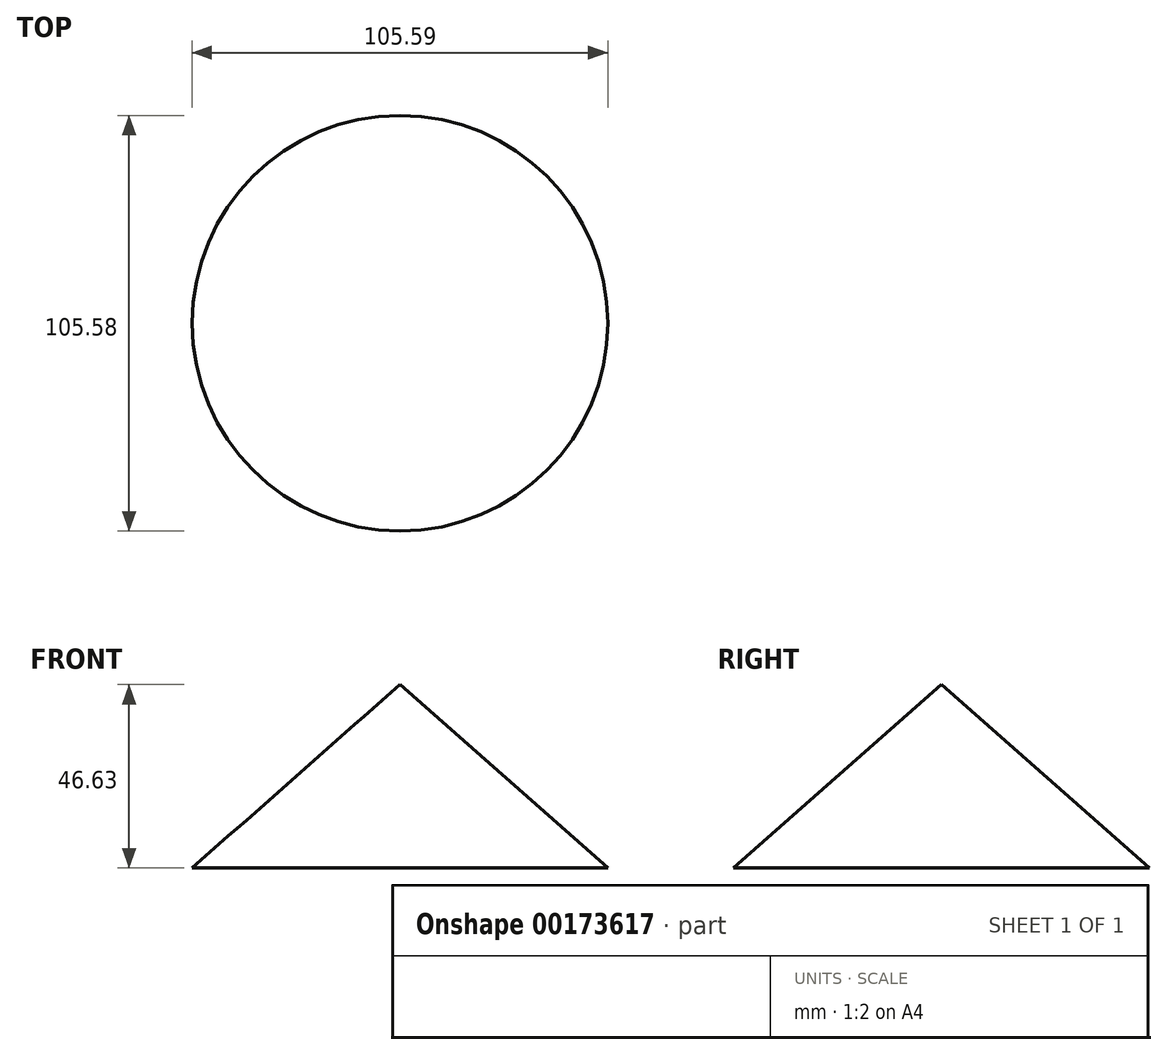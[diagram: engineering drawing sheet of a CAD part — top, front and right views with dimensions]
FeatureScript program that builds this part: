
annotation { "Feature Type Name" : "Feature", "Feature Type Description" : "" }
export const myFeature = defineFeature(function(context is Context, id is Id, definition is map)
    precondition{}
    {
        {
            var Q0;
            Q0=qCreatedBy(makeId("Front.planeOp"),FACE);
            var sketch = newSketch(context, id + "F0", { "sketchPlane" : qUnion([Q0])});
            skLineSegment(sketch, "E0", {"start": v(-52.8, 58.51) * mm, "end": v(-52.8, 11.88) * mm});
            skLineSegment(sketch, "E1", {"start": v(-52.8, 11.88) * mm, "end": v(0, 11.88) * mm});
            skLineSegment(sketch, "E2", {"start": v(-52.8, 58.51) * mm, "end": v(0, 11.88) * mm});
            skSolve(sketch);
        }
        {
            var Q0;
            Q0=makeQuery(id+"F0.imprint","IMPRINT",FACE,{"disambiguationData":[TD([[makeQuery(id+"F0.imprint","IMPRINT",EDGE,{"derivedFrom":sQuery(id+"F0.wireOp",EDGE,"E0")}),1.0]])]});
            var Q1;
            Q1=sQuery(id+"F0.wireOp",EDGE,"E0");
            revolve(context, id + "F1", {"entities" : qUnion([Q0]), "axis" : qUnion([Q1]), "revolveType" : RevolveType.FULL});
        }
    });
